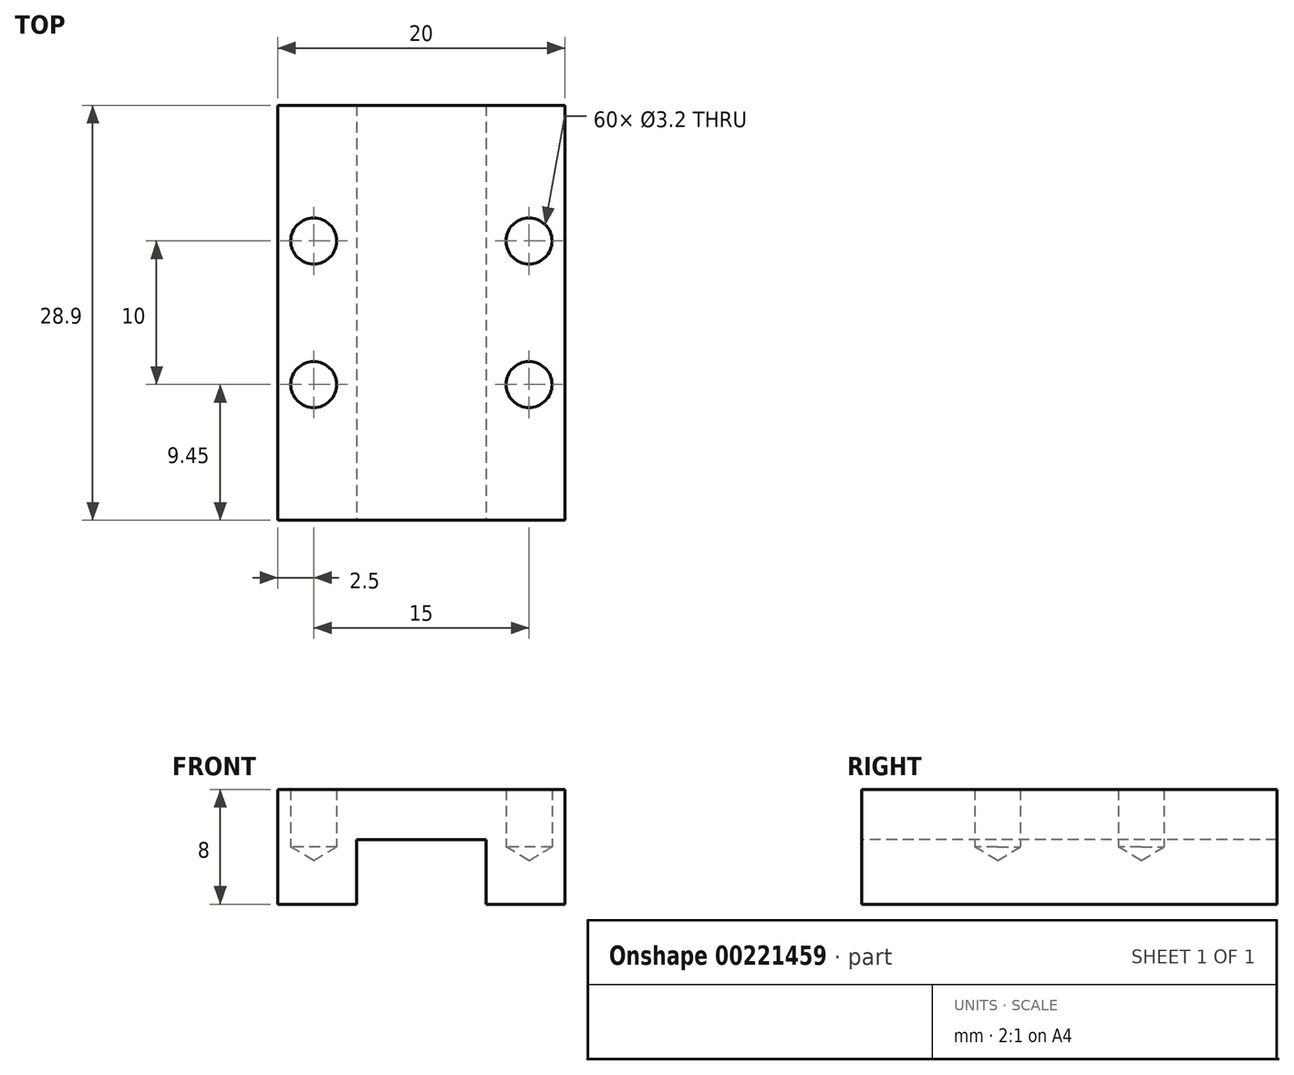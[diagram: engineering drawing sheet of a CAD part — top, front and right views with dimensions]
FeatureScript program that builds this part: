
annotation { "Feature Type Name" : "Feature", "Feature Type Description" : "" }
export const myFeature = defineFeature(function(context is Context, id is Id, definition is map)
    precondition{}
    {
        {
            var Q0;
            Q0=qCreatedBy(makeId("Top.planeOp"),FACE);
            var sketch = newSketch(context, id + "F0", { "sketchPlane" : qUnion([Q0])});
            skLineSegment(sketch, "E0.bottom", {"start": v(0, 0) * mm, "end": v(20, 0) * mm});
            skLineSegment(sketch, "E0.top", {"start": v(0, 28.9) * mm, "end": v(20, 28.9) * mm});
            skLineSegment(sketch, "E0.left", {"start": v(0, 0) * mm, "end": v(0, 28.9) * mm});
            skLineSegment(sketch, "E0.right", {"start": v(20, 0) * mm, "end": v(20, 28.9) * mm});
            skSolve(sketch);
        }
        {
            var Q0;
            Q0=makeQuery(id+"F0.imprint","IMPRINT",FACE,{"disambiguationData":[TD([[makeQuery(id+"F0.imprint","IMPRINT",EDGE,{"derivedFrom":sQuery(id+"F0.wireOp",EDGE,"E0.bottom")}),1.0]])]});
            extrude(context, id + "F1", {"entities" : qUnion([Q0]), "depth" : 8 * mm});
        }
        {
            var Q0;
            Q0=makeQuery(id+"F1.opExtrude","SWEPT_FACE",FACE,{"disambiguationData":[OSD([sQuery(id+"F0.wireOp",EDGE,"E0.bottom")])]});
            var sketch = newSketch(context, id + "F2", { "sketchPlane" : qUnion([Q0])});
            skLineSegment(sketch, "E1.bottom", {"start": v(5.5, 0) * mm, "end": v(14.5, 0) * mm});
            skLineSegment(sketch, "E1.top", {"start": v(5.5, 4.5) * mm, "end": v(14.5, 4.5) * mm});
            skLineSegment(sketch, "E1.left", {"start": v(5.5, 0) * mm, "end": v(5.5, 4.5) * mm});
            skLineSegment(sketch, "E1.right", {"start": v(14.5, 0) * mm, "end": v(14.5, 4.5) * mm});
            skLineSegment(sketch, "E2", {"start": v(10, 4.5) * mm, "end": v(10, 0) * mm, "construction": true});
            skSolve(sketch);
        }
        {
            var Q0;
            Q0=makeQuery(id+"F2.imprint","IMPRINT",FACE,{"disambiguationData":[TD([[makeQuery(id+"F2.imprint","IMPRINT",EDGE,{"derivedFrom":sQuery(id+"F2.wireOp",EDGE,"E1.bottom")}),1.0]])]});
            extrude(context, id + "F3", {"entities" : qUnion([Q0]), "operationType" : NewBodyOperationType.REMOVE, "endBound" : BoundingType.THROUGH_ALL, "oppositeDirection" : true, "depth" : 25 * mm});
        }
        {
            var Q0;
            Q0=makeQuery(id+"F1.opExtrude","CAP_FACE",FACE,{"disambiguationData":[OSD([sQuery(id+"F0.wireOp",EDGE,"E0.bottom"),sQuery(id+"F0.wireOp",EDGE,"E0.top"),sQuery(id+"F0.wireOp",EDGE,"E0.left"),sQuery(id+"F0.wireOp",EDGE,"E0.right")])],"isStart":false});
            var sketch = newSketch(context, id + "F4", { "sketchPlane" : qUnion([Q0])});
            skLineSegment(sketch, "E3.bottom", {"start": v(2.5, 19.45) * mm, "end": v(17.5, 19.45) * mm, "construction": true});
            skLineSegment(sketch, "E3.top", {"start": v(2.5, 9.45) * mm, "end": v(17.5, 9.45) * mm, "construction": true});
            skLineSegment(sketch, "E3.left", {"start": v(2.5, 19.45) * mm, "end": v(2.5, 9.45) * mm, "construction": true});
            skLineSegment(sketch, "E3.right", {"start": v(17.5, 19.45) * mm, "end": v(17.5, 9.45) * mm, "construction": true});
            skPoint(sketch, "E4", {"position": v(10, 28.9) * mm});
            skPoint(sketch, "E5", {"position": v(10, 19.45) * mm});
            skPoint(sketch, "E6", {"position": v(2.5, 14.45) * mm});
            skPoint(sketch, "E7", {"position": v(0, 14.45) * mm});
            skSolve(sketch);
        }
        {
            var Q0;
            Q0=sQuery(id+"F4.wireOp",VERTEX,"E3.left.end");
            var Q1;
            Q1=sQuery(id+"F4.wireOp",VERTEX,"E3.left.start");
            var Q2;
            Q2=sQuery(id+"F4.wireOp",VERTEX,"E3.bottom.end");
            var Q3;
            Q3=sQuery(id+"F4.wireOp",VERTEX,"E3.top.end");
            var Q4;
            Q4=makeQuery(id+"F1.opExtrude","SWEPT_BODY",BODY,{"disambiguationData":[OSD([sQuery(id+"F0.wireOp",EDGE,"E0.bottom"),sQuery(id+"F0.wireOp",EDGE,"E0.top"),sQuery(id+"F0.wireOp",EDGE,"E0.left"),sQuery(id+"F0.wireOp",EDGE,"E0.right")])]});
            hole(context, id + "F5", {"style" : HoleStyle.SIMPLE, "endStyle" : HoleEndStyle.BLIND, "standardTappedOrClearance" : lookupTablePath({ "standard" : "ISO", "size" : "3.2", "type" : "Drilled" }), "standardBlindInLast" : lookupTablePath({ "standard" : "ISO", "size" : "3.2", "type" : "Drilled" }), "holeDiameter" : 3.2 * mm, "holeDepth" : 4 * mm, "locations" : qUnion([Q0, Q1, Q2, Q3]), "scope" : qUnion([Q4])});
        }
    });
